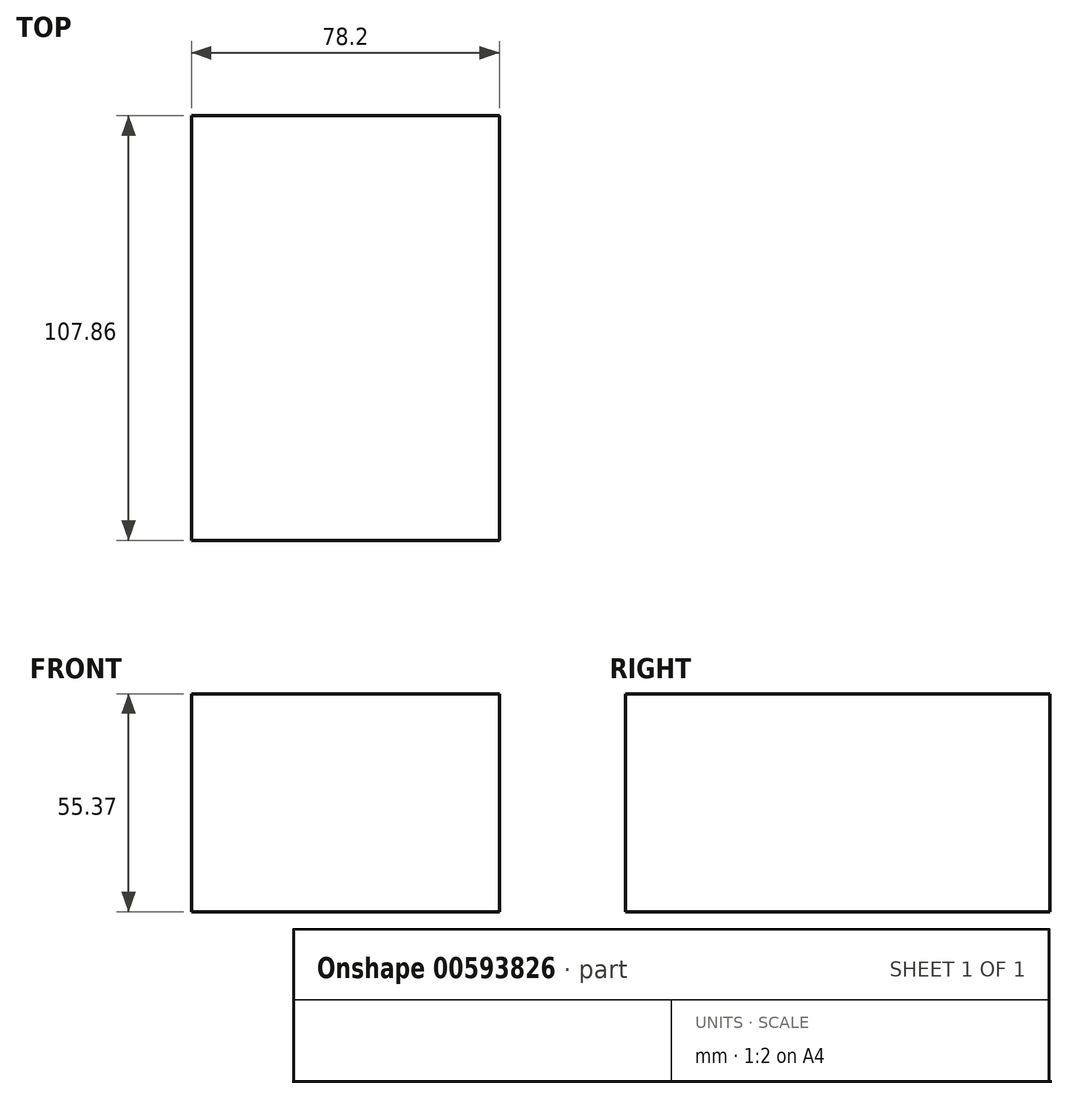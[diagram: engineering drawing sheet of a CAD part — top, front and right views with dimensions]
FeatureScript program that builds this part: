
annotation { "Feature Type Name" : "Feature", "Feature Type Description" : "" }
export const myFeature = defineFeature(function(context is Context, id is Id, definition is map)
    precondition{}
    {
        {
            var Q0;
            Q0=qCreatedBy(makeId("Top.planeOp"),FACE);
            var sketch = newSketch(context, id + "F0", { "sketchPlane" : qUnion([Q0])});
            skLineSegment(sketch, "E0.bottom", {"start": v(-37.02, 58.02) * mm, "end": v(41.18, 58.02) * mm});
            skLineSegment(sketch, "E0.top", {"start": v(-37.02, -49.84) * mm, "end": v(41.18, -49.84) * mm});
            skLineSegment(sketch, "E0.left", {"start": v(-37.02, 58.02) * mm, "end": v(-37.02, -49.84) * mm});
            skLineSegment(sketch, "E0.right", {"start": v(41.18, 58.02) * mm, "end": v(41.18, -49.84) * mm});
            skSolve(sketch);
        }
        {
            var Q0;
            Q0=makeQuery(id+"F0.imprint","IMPRINT",FACE,{"disambiguationData":[TD([[makeQuery(id+"F0.imprint","IMPRINT",EDGE,{"derivedFrom":sQuery(id+"F0.wireOp",EDGE,"E0.bottom")}),-1.0]])]});
            extrude(context, id + "F1", {"entities" : qUnion([Q0]), "depth" : 55.37 * mm, "offsetDistance" : 25.4 * mm});
        }
    });
